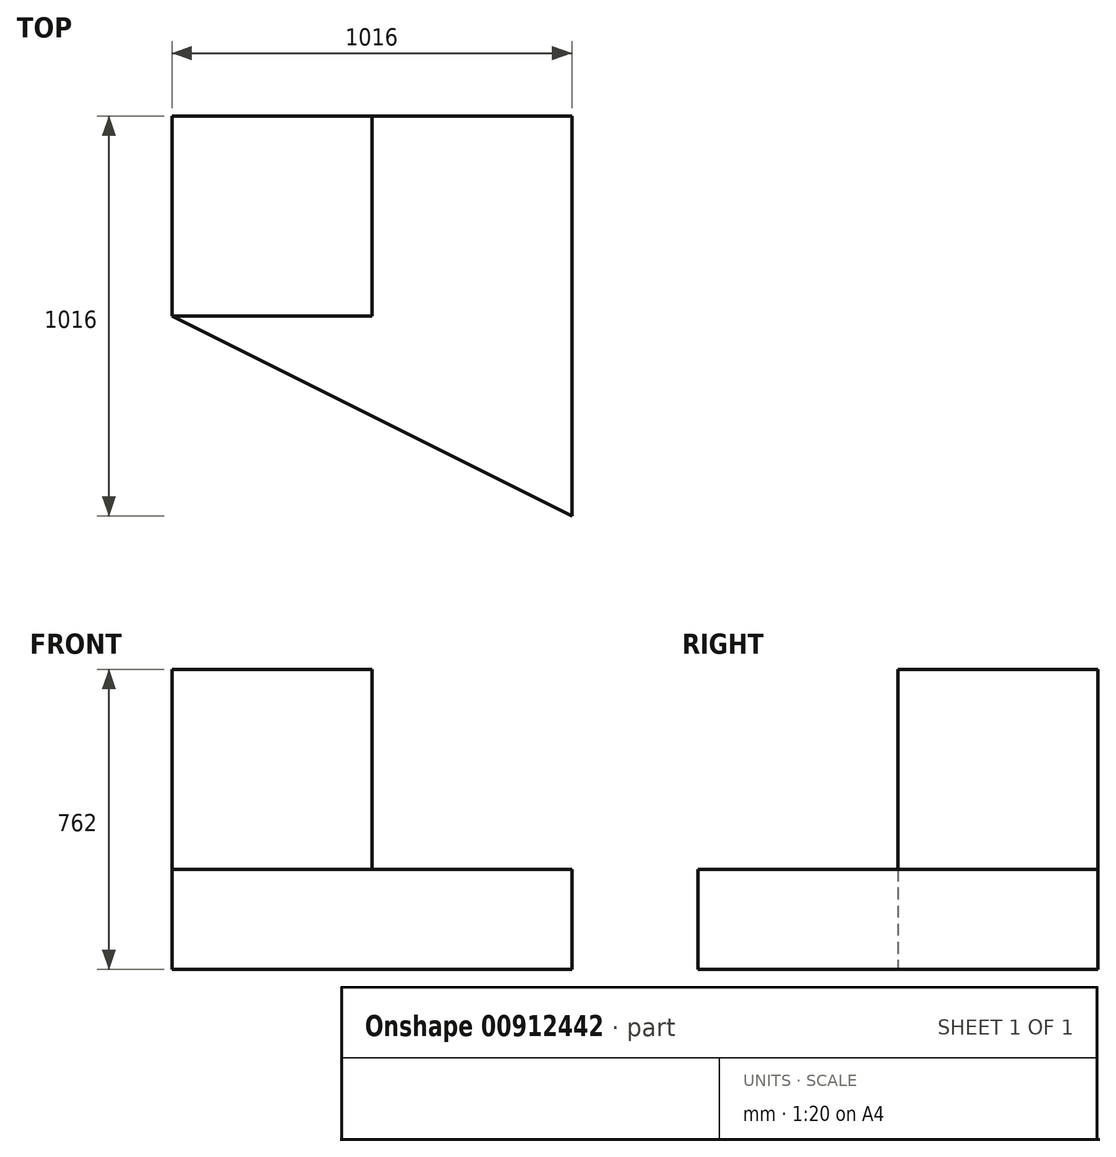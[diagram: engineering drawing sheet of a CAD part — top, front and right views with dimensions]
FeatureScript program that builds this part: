
annotation { "Feature Type Name" : "Feature", "Feature Type Description" : "" }
export const myFeature = defineFeature(function(context is Context, id is Id, definition is map)
    precondition{}
    {
        {
            var Q0;
            Q0=qCreatedBy(makeId("Top.planeOp"),FACE);
            var sketch = newSketch(context, id + "F0", { "sketchPlane" : qUnion([Q0])});
            skLineSegment(sketch, "E0.top", {"start": v(0, 508) * mm, "end": v(1016, 508) * mm});
            skLineSegment(sketch, "E0.left", {"start": v(0, 0) * mm, "end": v(0, 508) * mm});
            skLineSegment(sketch, "E0.right", {"start": v(1016, -508) * mm, "end": v(1016, 508) * mm});
            skLineSegment(sketch, "E1", {"start": v(0, 0) * mm, "end": v(508, 0) * mm});
            skLineSegment(sketch, "E2", {"start": v(508, 0) * mm, "end": v(508, 508) * mm});
            skLineSegment(sketch, "E3", {"start": v(0, 0) * mm, "end": v(1016, -508) * mm});
            skSolve(sketch);
        }
        {
            var Q0;
            {var subQ0=sQuery(id+"F0.wireOp",EDGE,"E0.left");Q0=makeQuery(id+"F0.imprint","IMPRINT",FACE,{"disambiguationData":[TD([[makeQuery(id+"F0.imprint","IMPRINT",EDGE,{"derivedFrom":subQ0}),-1.0]])]});}
            extrude(context, id + "F1", {"entities" : qUnion([Q0]), "depth" : 762 * mm, "offsetDistance" : 25.4 * mm});
        }
        {
            var Q0;
            {var subQ1=sQuery(id+"F0.wireOp",EDGE,"E0.right");Q0=makeQuery(id+"F0.imprint","IMPRINT",FACE,{"disambiguationData":[TD([[makeQuery(id+"F0.imprint","IMPRINT",EDGE,{"derivedFrom":subQ1}),1.0]])]});}
            extrude(context, id + "F2", {"entities" : qUnion([Q0]), "operationType" : NewBodyOperationType.ADD, "depth" : 254 * mm, "offsetDistance" : 25.4 * mm});
        }
    });
